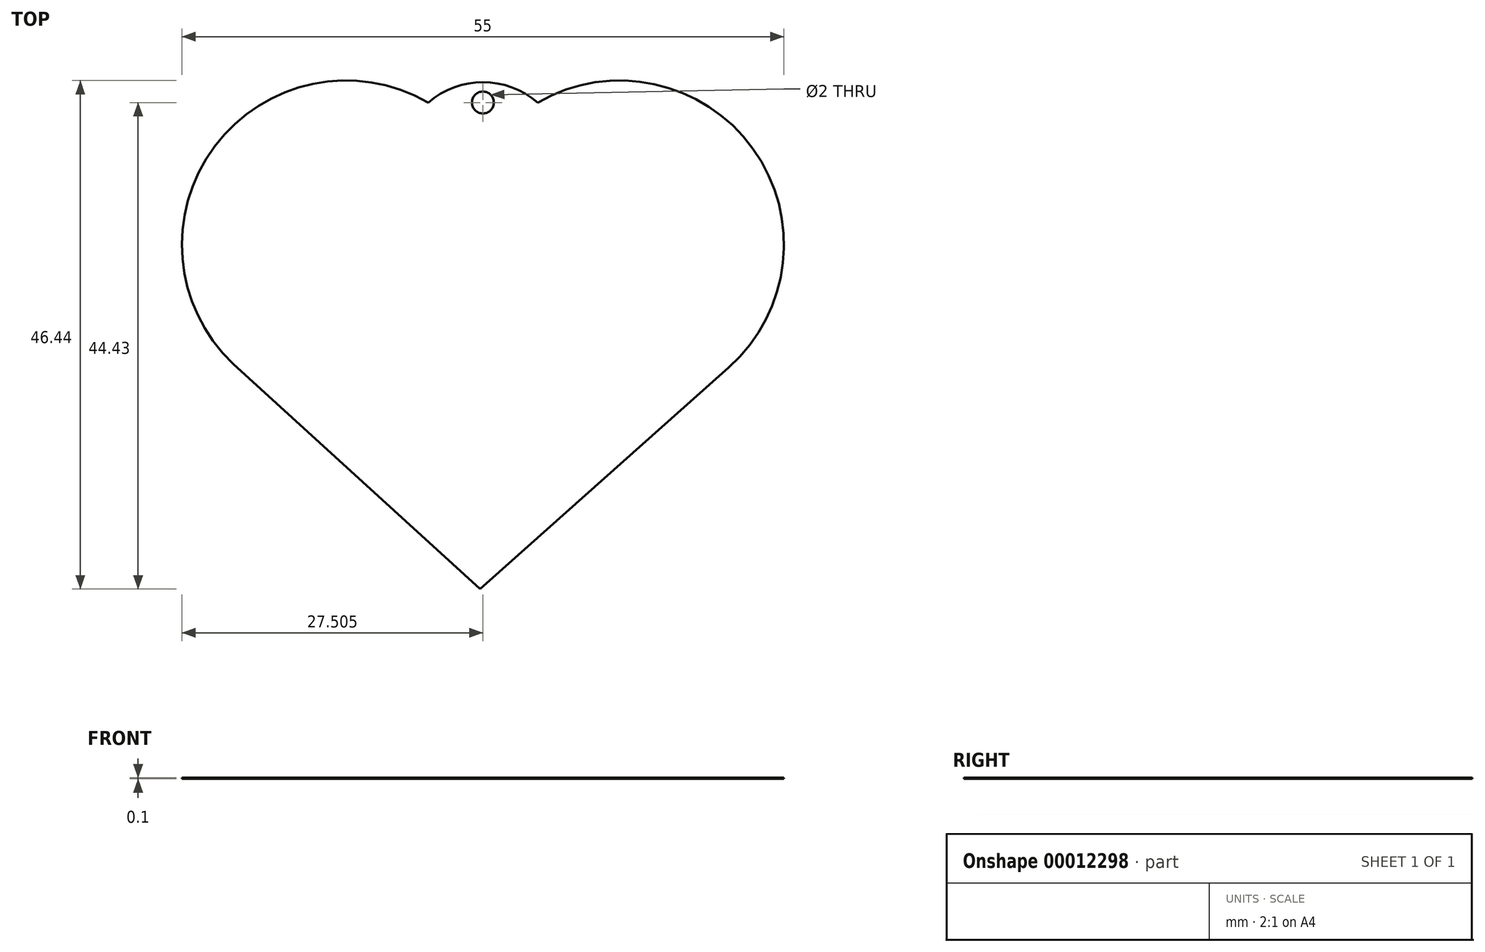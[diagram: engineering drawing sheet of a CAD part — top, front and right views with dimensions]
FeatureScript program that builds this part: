
annotation { "Feature Type Name" : "Feature", "Feature Type Description" : "" }
export const myFeature = defineFeature(function(context is Context, id is Id, definition is map)
    precondition{}
    {
        {
            var Q0;
            Q0=qCreatedBy(makeId("Top.planeOp"),FACE);
            var sketch = newSketch(context, id + "F0", { "sketchPlane" : qUnion([Q0])});
            skLineSegment(sketch, "E0", {"start": v(-12.32, -31.44) * mm, "end": v(-34.88, -10.89) * mm});
            skArc(sketch, "E1.trimOffspring", {"start": v(10.38, -11.23) * mm, "mid": v(12.6, 8.76) * mm, "end": v(-7.07, 13) * mm});
            skArc(sketch, "E2", {"start": v(-17.07, 13) * mm, "mid": v(-36.59, 8.97) * mm, "end": v(-34.88, -10.89) * mm});
            skLineSegment(sketch, "E3", {"start": v(-12.32, -31.44) * mm, "end": v(10.38, -11.23) * mm});
            skArc(sketch, "E4", {"start": v(-7.07, 13) * mm, "mid": v(-12.07, 14.84) * mm, "end": v(-17.07, 13) * mm});
            skCircle(sketch, "E5", {"center": v(-12.07, 13) * mm, "radius": 1 * mm});
            skSolve(sketch);
        }
        {
            var Q0;
            Q0=makeQuery(id+"F0.imprint","IMPRINT",FACE,{"disambiguationData":[TD([[makeQuery(id+"F0.imprint","IMPRINT",EDGE,{"derivedFrom":sQuery(id+"F0.wireOp",EDGE,"E0")}),-1.0]])]});
            extrude(context, id + "F1", {"entities" : qUnion([Q0]), "depth" : 0.1 * mm});
        }
    });
